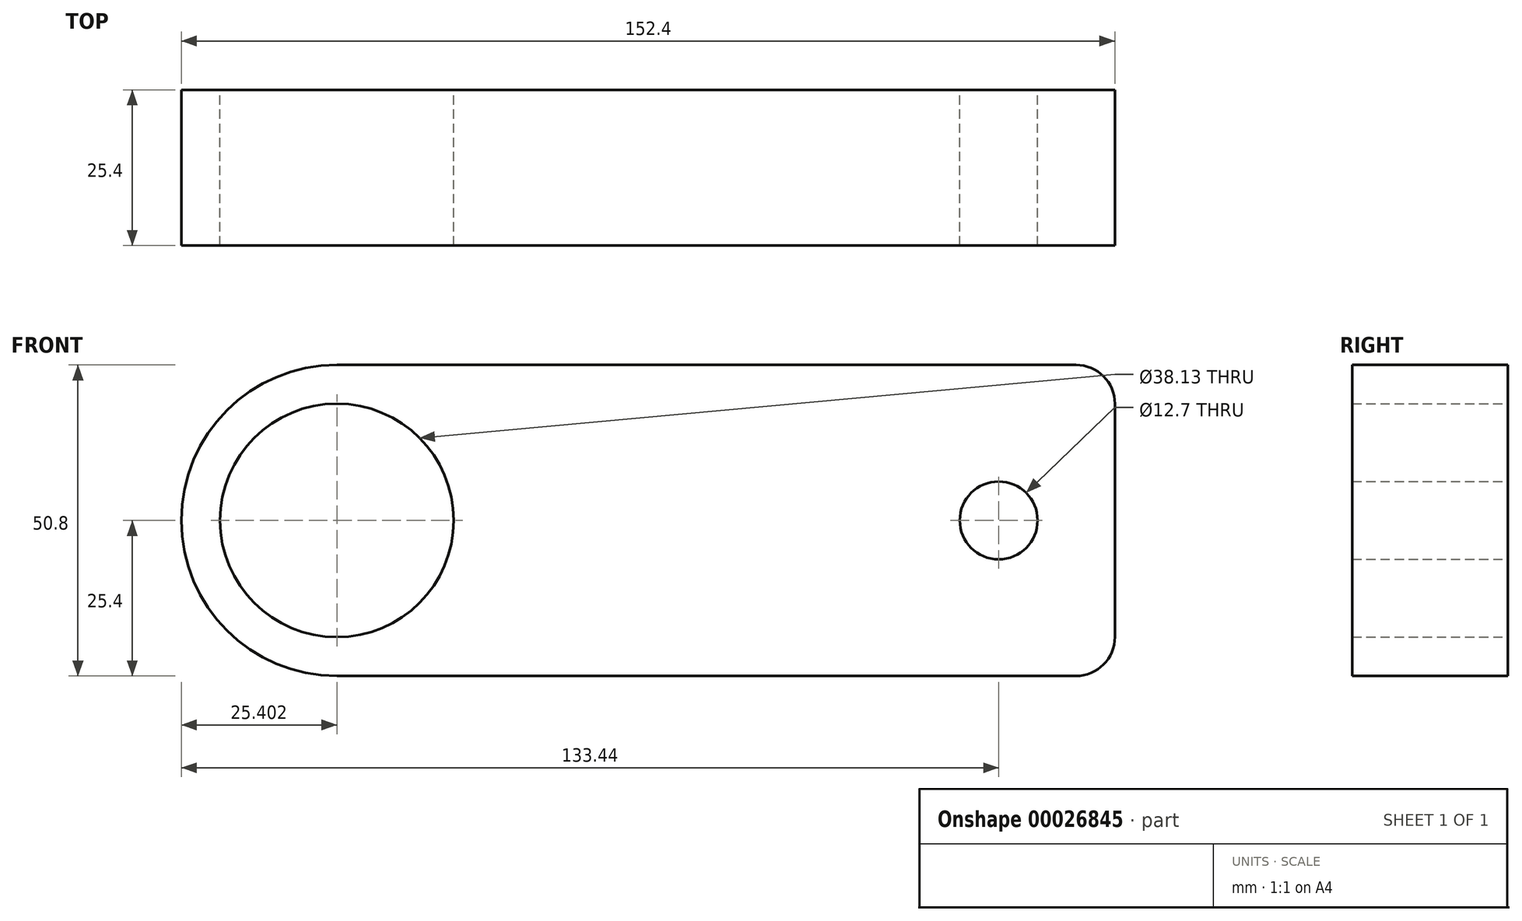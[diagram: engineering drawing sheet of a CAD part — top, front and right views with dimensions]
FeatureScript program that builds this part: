
annotation { "Feature Type Name" : "Feature", "Feature Type Description" : "" }
export const myFeature = defineFeature(function(context is Context, id is Id, definition is map)
    precondition{}
    {
        {
            var Q0;
            Q0=qCreatedBy(makeId("Front.planeOp"),FACE);
            var sketch = newSketch(context, id + "F0", { "sketchPlane" : qUnion([Q0])});
            skLineSegment(sketch, "E0.bottom", {"start": v(-42.23, 25.4) * mm, "end": v(78.42, 25.4) * mm});
            skLineSegment(sketch, "E0.top", {"start": v(-42.23, -25.4) * mm, "end": v(78.42, -25.4) * mm});
            skLineSegment(sketch, "E0.left", {"start": v(-67.63, 0) * mm, "end": v(-67.63, 0) * mm});
            skLineSegment(sketch, "E0.right", {"start": v(84.77, 19.05) * mm, "end": v(84.77, -19.05) * mm});
            skCircle(sketch, "E1", {"center": v(-42.23, 0) * mm, "radius": 19.06 * mm});
            skPoint(sketch, "E2.visualSharp", {"position": v(-67.63, 25.4) * mm});
            skArc(sketch, "E2.filletArc", {"start": v(-42.23, 25.4) * mm, "mid": v(-60.19, 17.96) * mm, "end": v(-67.63, 0) * mm});
            skPoint(sketch, "E3.visualSharp", {"position": v(84.77, 25.4) * mm});
            skArc(sketch, "E3.filletArc", {"start": v(84.77, 19.05) * mm, "mid": v(82.91, 23.54) * mm, "end": v(78.42, 25.4) * mm});
            skPoint(sketch, "E4.visualSharp", {"position": v(84.77, -25.4) * mm});
            skArc(sketch, "E4.filletArc", {"start": v(78.42, -25.4) * mm, "mid": v(82.91, -23.54) * mm, "end": v(84.77, -19.05) * mm});
            skPoint(sketch, "E5.visualSharp", {"position": v(-67.63, -25.4) * mm});
            skArc(sketch, "E5.filletArc", {"start": v(-67.63, 0) * mm, "mid": v(-60.19, -17.96) * mm, "end": v(-42.23, -25.4) * mm});
            skPoint(sketch, "E6", {"position": v(65.8, 0) * mm});
            skCircle(sketch, "E7", {"center": v(65.8, 0) * mm, "radius": 6.35 * mm});
            skSolve(sketch);
        }
        {
            var Q0;
            Q0=makeQuery(id+"F0.imprint","IMPRINT",FACE,{"disambiguationData":[TD([[makeQuery(id+"F0.imprint","IMPRINT",EDGE,{"derivedFrom":sQuery(id+"F0.wireOp",EDGE,"E0.bottom")}),-1.0]])]});
            extrude(context, id + "F1", {"entities" : qUnion([Q0]), "endBound" : BoundingType.SYMMETRIC, "depth" : 25.4 * mm});
        }
    });
